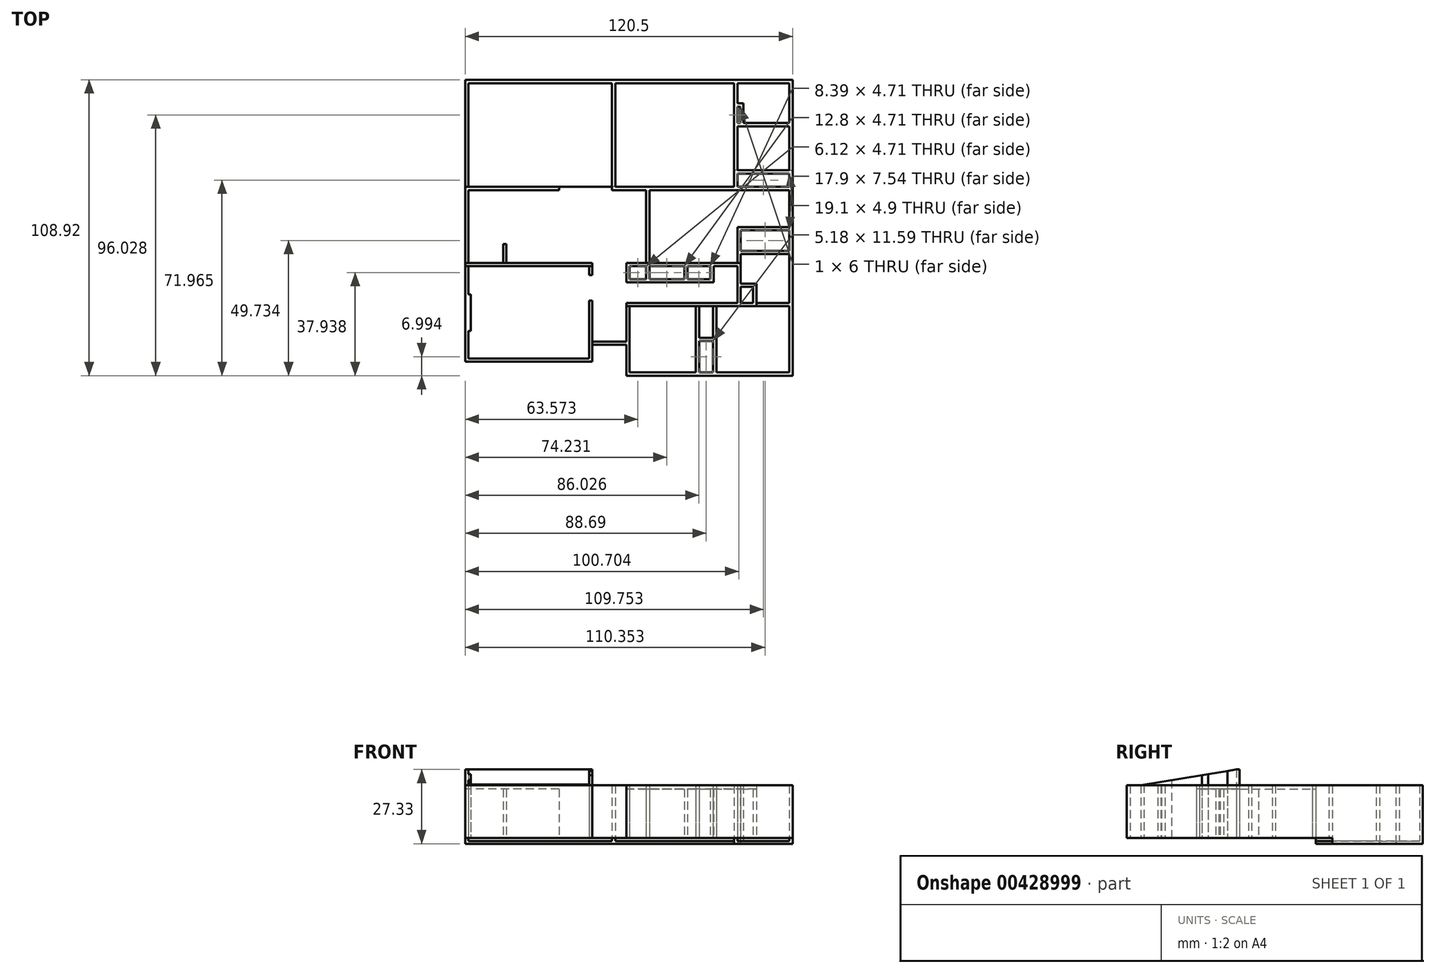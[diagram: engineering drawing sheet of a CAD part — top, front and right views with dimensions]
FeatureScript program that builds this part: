
annotation { "Feature Type Name" : "Feature", "Feature Type Description" : "" }
export const myFeature = defineFeature(function(context is Context, id is Id, definition is map)
    precondition{}
    {
        {
            assignVariable(context, id + "F0", {"name" : "scale", "anyValue" : 125});
        }
        {
            assignVariable(context, id + "F1", {"name" : "sink_depth", "anyValue" : 152.4 * mm / getVariable(context, 'scale')});
        }
        {
            assignVariable(context, id + "F2", {"name" : "ceil_low", "anyValue" : 2247.9 * mm / getVariable(context, 'scale')});
        }
        {
            assignVariable(context, id + "F3", {"name" : "ceil_high", "anyValue" : 2425.7 * mm / getVariable(context, 'scale')});
        }
        {
            assignVariable(context, id + "F4", {"name" : "ceil_max", "anyValue" : (3048 * mm + 101.6 * mm) / getVariable(context, 'scale')});
        }
        {
            var Q0;
            Q0=qCreatedBy(makeId("Top.planeOp"),FACE);
            var sketch = newSketch(context, id + "F5", { "sketchPlane" : qUnion([Q0])});
            skLineSegment(sketch, "E0", {"start": v(0, 0) * mm, "end": v(0, 103.76) * mm});
            skLineSegment(sketch, "E1", {"start": v(0, 103.76) * mm, "end": v(120.5, 103.76) * mm});
            skLineSegment(sketch, "E2", {"start": v(120.5, 103.76) * mm, "end": v(120.5, -5.16) * mm});
            skLineSegment(sketch, "E3", {"start": v(120.5, -5.16) * mm, "end": v(59.32, -5.16) * mm});
            skLineSegment(sketch, "E4", {"start": v(1.2, 1.2) * mm, "end": v(45.6, 1.2) * mm});
            skLineSegment(sketch, "E5", {"start": v(45.6, 1.2) * mm, "end": v(45.6, 22.43) * mm});
            skLineSegment(sketch, "E6", {"start": v(45.6, 22.43) * mm, "end": v(46.8, 22.43) * mm});
            skLineSegment(sketch, "E7", {"start": v(46.8, 22.43) * mm, "end": v(46.8, 7.4) * mm});
            skLineSegment(sketch, "E8", {"start": v(59.32, -3.96) * mm, "end": v(59.32, 6.2) * mm});
            skLineSegment(sketch, "E9", {"start": v(59.32, 21.62) * mm, "end": v(100.2, 21.62) * mm});
            skLineSegment(sketch, "E10", {"start": v(86.1, -3.96) * mm, "end": v(84.9, -3.96) * mm, "construction": true});
            skLineSegment(sketch, "E11", {"start": v(84.9, -3.96) * mm, "end": v(84.9, 20.42) * mm});
            skLineSegment(sketch, "E12", {"start": v(84.9, 20.42) * mm, "end": v(60.52, 20.42) * mm});
            skLineSegment(sketch, "E13", {"start": v(60.52, 20.42) * mm, "end": v(60.52, -3.96) * mm});
            skLineSegment(sketch, "E14", {"start": v(60.52, -3.96) * mm, "end": v(84.9, -3.96) * mm});
            skLineSegment(sketch, "E15", {"start": v(59.32, -3.96) * mm, "end": v(60.52, -3.96) * mm, "construction": true});
            skLineSegment(sketch, "E16", {"start": v(60.52, 20.42) * mm, "end": v(60.52, 21.62) * mm, "construction": true});
            skLineSegment(sketch, "E17", {"start": v(86.1, 20.42) * mm, "end": v(91.28, 20.42) * mm});
            skLineSegment(sketch, "E18", {"start": v(119.3, 20.42) * mm, "end": v(119.3, -3.96) * mm});
            skLineSegment(sketch, "E19", {"start": v(46.8, 1.2) * mm, "end": v(46.8, 0) * mm});
            skLineSegment(sketch, "E20", {"start": v(1.2, 1.2) * mm, "end": v(0, 1.2) * mm, "construction": true});
            skLineSegment(sketch, "E21", {"start": v(1.2, 1.2) * mm, "end": v(1.2, 35.13) * mm});
            skLineSegment(sketch, "E22", {"start": v(1.2, 35.13) * mm, "end": v(45.6, 35.13) * mm});
            skLineSegment(sketch, "E23", {"start": v(45.6, 35.13) * mm, "end": v(45.6, 31.86) * mm});
            skLineSegment(sketch, "E24", {"start": v(45.6, 31.86) * mm, "end": v(46.8, 31.86) * mm});
            skLineSegment(sketch, "E25", {"start": v(46.8, 31.86) * mm, "end": v(46.8, 36.33) * mm});
            skLineSegment(sketch, "E26", {"start": v(15.2, 36.33) * mm, "end": v(15.2, 43.34) * mm});
            skLineSegment(sketch, "E27", {"start": v(15.2, 43.34) * mm, "end": v(14, 43.34) * mm});
            skLineSegment(sketch, "E28", {"start": v(14, 43.34) * mm, "end": v(14, 36.33) * mm});
            skLineSegment(sketch, "E29", {"start": v(14, 36.33) * mm, "end": v(1.2, 36.33) * mm});
            skLineSegment(sketch, "E30", {"start": v(1.2, 36.33) * mm, "end": v(1.2, 63.16) * mm});
            skLineSegment(sketch, "E31", {"start": v(1.2, 63.16) * mm, "end": v(34.52, 63.16) * mm});
            skLineSegment(sketch, "E32", {"start": v(34.52, 63.16) * mm, "end": v(34.52, 64.36) * mm});
            skLineSegment(sketch, "E33", {"start": v(34.52, 64.36) * mm, "end": v(1.2, 64.36) * mm});
            skLineSegment(sketch, "E34", {"start": v(1.2, 64.36) * mm, "end": v(1.2, 102.56) * mm});
            skLineSegment(sketch, "E35", {"start": v(1.2, 102.56) * mm, "end": v(54.03, 102.56) * mm});
            skLineSegment(sketch, "E36", {"start": v(1.2, 36.33) * mm, "end": v(1.2, 35.13) * mm, "construction": true});
            skLineSegment(sketch, "E37", {"start": v(46.8, 36.33) * mm, "end": v(15.2, 36.33) * mm});
            skLineSegment(sketch, "E38", {"start": v(54.03, 102.56) * mm, "end": v(54.03, 63.16) * mm});
            skLineSegment(sketch, "E39", {"start": v(54.03, 63.16) * mm, "end": v(66.63, 63.16) * mm});
            skLineSegment(sketch, "E40", {"start": v(66.63, 63.16) * mm, "end": v(66.63, 36.33) * mm});
            skLineSegment(sketch, "E41", {"start": v(66.63, 36.33) * mm, "end": v(59.32, 36.33) * mm});
            skLineSegment(sketch, "E42", {"start": v(59.32, 36.33) * mm, "end": v(59.32, 29.22) * mm});
            skLineSegment(sketch, "E43", {"start": v(1.2, 102.56) * mm, "end": v(1.2, 103.76) * mm, "construction": true});
            skLineSegment(sketch, "E44", {"start": v(54.03, 102.56) * mm, "end": v(55.23, 102.56) * mm, "construction": true});
            skLineSegment(sketch, "E45", {"start": v(55.23, 102.56) * mm, "end": v(99, 102.56) * mm});
            skLineSegment(sketch, "E46", {"start": v(99, 102.56) * mm, "end": v(99, 64.36) * mm});
            skLineSegment(sketch, "E47", {"start": v(99, 64.36) * mm, "end": v(55.23, 64.36) * mm});
            skLineSegment(sketch, "E48", {"start": v(55.23, 64.36) * mm, "end": v(55.23, 102.56) * mm});
            skLineSegment(sketch, "E49", {"start": v(100.2, 102.56) * mm, "end": v(119.3, 102.56) * mm});
            skLineSegment(sketch, "E50", {"start": v(119.3, 102.56) * mm, "end": v(119.3, 87.87) * mm});
            skLineSegment(sketch, "E51", {"start": v(119.3, 86.67) * mm, "end": v(102.4, 86.67) * mm});
            skLineSegment(sketch, "E52", {"start": v(102.4, 87.87) * mm, "end": v(102.4, 95.07) * mm});
            skLineSegment(sketch, "E53", {"start": v(102.4, 95.07) * mm, "end": v(100.2, 95.07) * mm});
            skLineSegment(sketch, "E54", {"start": v(100.2, 95.07) * mm, "end": v(100.2, 102.56) * mm});
            skLineSegment(sketch, "E55", {"start": v(99, 93.87) * mm, "end": v(101.2, 93.87) * mm});
            skLineSegment(sketch, "E56", {"start": v(101.2, 93.87) * mm, "end": v(101.2, 87.87) * mm});
            skLineSegment(sketch, "E57", {"start": v(101.2, 87.87) * mm, "end": v(99, 87.87) * mm});
            skLineSegment(sketch, "E58", {"start": v(100.2, 102.56) * mm, "end": v(99, 102.56) * mm, "construction": true});
            skLineSegment(sketch, "E59", {"start": v(101.2, 93.87) * mm, "end": v(102.4, 93.87) * mm, "construction": true});
            skLineSegment(sketch, "E60", {"start": v(101.2, 93.87) * mm, "end": v(101.2, 95.07) * mm, "construction": true});
            skLineSegment(sketch, "E61", {"start": v(102.4, 86.67) * mm, "end": v(100.2, 86.67) * mm});
            skLineSegment(sketch, "E62", {"start": v(100.2, 86.67) * mm, "end": v(100.2, 70.45) * mm});
            skLineSegment(sketch, "E63", {"start": v(101.2, 87.87) * mm, "end": v(101.2, 86.67) * mm, "construction": true});
            skLineSegment(sketch, "E64", {"start": v(34.52, 63.16) * mm, "end": v(54.03, 63.16) * mm, "construction": true});
            skLineSegment(sketch, "E65", {"start": v(46.8, 36.33) * mm, "end": v(59.32, 36.33) * mm, "construction": true});
            skLineSegment(sketch, "E66", {"start": v(102.4, 87.87) * mm, "end": v(119.3, 87.87) * mm});
            skLineSegment(sketch, "E67", {"start": v(119.3, 86.67) * mm, "end": v(119.3, 70.45) * mm});
            skLineSegment(sketch, "E68", {"start": v(119.3, 70.45) * mm, "end": v(100.2, 70.45) * mm});
            skLineSegment(sketch, "E69", {"start": v(100.2, 70.45) * mm, "end": v(100.2, 69.25) * mm, "construction": true});
            skLineSegment(sketch, "E70", {"start": v(100.2, 69.25) * mm, "end": v(100.2, 64.36) * mm});
            skLineSegment(sketch, "E71", {"start": v(100.2, 64.36) * mm, "end": v(119.3, 64.36) * mm});
            skLineSegment(sketch, "E72", {"start": v(119.3, 64.36) * mm, "end": v(119.3, 69.25) * mm});
            skLineSegment(sketch, "E73", {"start": v(119.3, 69.25) * mm, "end": v(100.2, 69.25) * mm});
            skLineSegment(sketch, "E74", {"start": v(119.3, 63.16) * mm, "end": v(119.3, 49.54) * mm});
            skLineSegment(sketch, "E75", {"start": v(59.32, 29.22) * mm, "end": v(91.42, 29.22) * mm});
            skLineSegment(sketch, "E76", {"start": v(60.52, 35.13) * mm, "end": v(60.52, 30.42) * mm});
            skLineSegment(sketch, "E77", {"start": v(60.52, 30.42) * mm, "end": v(66.63, 30.42) * mm});
            skLineSegment(sketch, "E78", {"start": v(66.63, 30.42) * mm, "end": v(66.63, 35.13) * mm});
            skLineSegment(sketch, "E79", {"start": v(66.63, 35.13) * mm, "end": v(60.52, 35.13) * mm});
            skLineSegment(sketch, "E80", {"start": v(60.52, 35.13) * mm, "end": v(60.52, 36.33) * mm, "construction": true});
            skLineSegment(sketch, "E81", {"start": v(60.52, 35.13) * mm, "end": v(59.32, 35.13) * mm, "construction": true});
            skLineSegment(sketch, "E82", {"start": v(60.52, 30.42) * mm, "end": v(60.52, 29.22) * mm, "construction": true});
            skLineSegment(sketch, "E83", {"start": v(67.83, 63.16) * mm, "end": v(67.83, 36.33) * mm});
            skLineSegment(sketch, "E84", {"start": v(67.83, 36.33) * mm, "end": v(100.2, 36.33) * mm});
            skLineSegment(sketch, "E85", {"start": v(91.42, 29.22) * mm, "end": v(91.42, 35.13) * mm});
            skLineSegment(sketch, "E86", {"start": v(91.42, 35.13) * mm, "end": v(100.2, 35.13) * mm});
            skLineSegment(sketch, "E87", {"start": v(100.2, 35.13) * mm, "end": v(100.2, 21.62) * mm});
            skLineSegment(sketch, "E88", {"start": v(119.3, 102.56) * mm, "end": v(120.5, 102.56) * mm, "construction": true});
            skLineSegment(sketch, "E89", {"start": v(66.63, 36.33) * mm, "end": v(67.83, 36.33) * mm, "construction": true});
            skLineSegment(sketch, "E90", {"start": v(100.2, 36.33) * mm, "end": v(100.2, 35.13) * mm, "construction": true});
            skLineSegment(sketch, "E91", {"start": v(67.83, 35.13) * mm, "end": v(80.63, 35.13) * mm});
            skLineSegment(sketch, "E92", {"start": v(90.22, 35.13) * mm, "end": v(90.22, 30.42) * mm});
            skLineSegment(sketch, "E93", {"start": v(90.22, 30.42) * mm, "end": v(81.83, 30.42) * mm});
            skLineSegment(sketch, "E94", {"start": v(67.83, 30.42) * mm, "end": v(67.83, 35.13) * mm});
            skLineSegment(sketch, "E95", {"start": v(67.83, 63.16) * mm, "end": v(119.3, 63.16) * mm});
            skLineSegment(sketch, "E96", {"start": v(99, 64.36) * mm, "end": v(99, 63.16) * mm, "construction": true});
            skLineSegment(sketch, "E97", {"start": v(92.48, 20.42) * mm, "end": v(92.48, -3.96) * mm});
            skLineSegment(sketch, "E98", {"start": v(91.28, 20.42) * mm, "end": v(92.48, 20.42) * mm});
            skLineSegment(sketch, "E99", {"start": v(92.48, 20.42) * mm, "end": v(119.3, 20.42) * mm});
            skLineSegment(sketch, "E100.bottom", {"start": v(101.4, 21.62) * mm, "end": v(106.01, 21.62) * mm});
            skLineSegment(sketch, "E100.top", {"start": v(101.4, 27.51) * mm, "end": v(106.01, 27.51) * mm});
            skLineSegment(sketch, "E100.left", {"start": v(101.4, 21.62) * mm, "end": v(101.4, 27.51) * mm});
            skLineSegment(sketch, "E100.right", {"start": v(106.01, 21.62) * mm, "end": v(106.01, 27.51) * mm});
            skLineSegment(sketch, "E101", {"start": v(101.4, 28.71) * mm, "end": v(101.4, 39.6) * mm});
            skLineSegment(sketch, "E102", {"start": v(101.4, 39.6) * mm, "end": v(119.3, 39.6) * mm});
            skLineSegment(sketch, "E103", {"start": v(119.3, 39.6) * mm, "end": v(119.3, 21.62) * mm});
            skLineSegment(sketch, "E104", {"start": v(119.3, 21.62) * mm, "end": v(107.21, 21.62) * mm});
            skLineSegment(sketch, "E105", {"start": v(107.21, 21.62) * mm, "end": v(107.21, 28.71) * mm});
            skLineSegment(sketch, "E106", {"start": v(101.4, 28.71) * mm, "end": v(107.21, 28.71) * mm});
            skLineSegment(sketch, "E107", {"start": v(106.01, 27.51) * mm, "end": v(107.21, 27.51) * mm, "construction": true});
            skLineSegment(sketch, "E108", {"start": v(106.01, 27.51) * mm, "end": v(106.01, 28.71) * mm, "construction": true});
            skLineSegment(sketch, "E109.bottom", {"start": v(101.4, 40.8) * mm, "end": v(119.3, 40.8) * mm});
            skLineSegment(sketch, "E109.top", {"start": v(101.4, 48.34) * mm, "end": v(119.3, 48.34) * mm});
            skLineSegment(sketch, "E109.left", {"start": v(101.4, 40.8) * mm, "end": v(101.4, 48.34) * mm});
            skLineSegment(sketch, "E109.right", {"start": v(119.3, 40.8) * mm, "end": v(119.3, 48.34) * mm});
            skLineSegment(sketch, "E110", {"start": v(119.3, 40.8) * mm, "end": v(119.3, 39.6) * mm, "construction": true});
            skLineSegment(sketch, "E111", {"start": v(119.3, 49.54) * mm, "end": v(119.3, 48.34) * mm, "construction": true});
            skLineSegment(sketch, "E112", {"start": v(100.2, 21.62) * mm, "end": v(101.4, 21.62) * mm, "construction": true});
            skLineSegment(sketch, "E113", {"start": v(81.83, 35.13) * mm, "end": v(81.83, 30.42) * mm});
            skLineSegment(sketch, "E114", {"start": v(80.63, 30.42) * mm, "end": v(80.63, 30.42) * mm});
            skLineSegment(sketch, "E115", {"start": v(81.83, 35.13) * mm, "end": v(90.22, 35.13) * mm});
            skLineSegment(sketch, "E116", {"start": v(80.63, 35.13) * mm, "end": v(81.83, 35.13) * mm, "construction": true});
            skLineSegment(sketch, "E117", {"start": v(90.22, 35.13) * mm, "end": v(91.42, 35.13) * mm, "construction": true});
            skLineSegment(sketch, "E118", {"start": v(120.5, -5.16) * mm, "end": v(120.5, -45.16) * mm});
            skLineSegment(sketch, "E119", {"start": v(120.5, -45.16) * mm, "end": v(59.32, -45.16) * mm});
            skLineSegment(sketch, "E120", {"start": v(59.32, -45.16) * mm, "end": v(59.32, -5.16) * mm});
            skLineSegment(sketch, "E121", {"start": v(60.52, -5.16) * mm, "end": v(60.52, -43.96) * mm});
            skLineSegment(sketch, "E122", {"start": v(60.52, -43.96) * mm, "end": v(119.3, -43.96) * mm});
            skLineSegment(sketch, "E123", {"start": v(119.3, -43.96) * mm, "end": v(119.3, -5.16) * mm});
            skLineSegment(sketch, "E124", {"start": v(60.52, -43.96) * mm, "end": v(60.52, -45.16) * mm, "construction": true});
            skLineSegment(sketch, "E125", {"start": v(60.52, -43.96) * mm, "end": v(59.32, -43.96) * mm, "construction": true});
            skLineSegment(sketch, "E126", {"start": v(59.32, -3.96) * mm, "end": v(59.32, -5.16) * mm});
            skLineSegment(sketch, "E127.trimOffspring", {"start": v(46.8, 0) * mm, "end": v(0, 0) * mm});
            skLineSegment(sketch, "E128", {"start": v(46.8, 6.2) * mm, "end": v(59.32, 6.2) * mm});
            skLineSegment(sketch, "E129", {"start": v(59.32, 7.4) * mm, "end": v(46.8, 7.4) * mm});
            skLineSegment(sketch, "E130", {"start": v(46.8, 7.4) * mm, "end": v(46.8, 6.2) * mm, "construction": true});
            skLineSegment(sketch, "E131", {"start": v(46.8, 6.2) * mm, "end": v(46.8, 1.2) * mm});
            skLineSegment(sketch, "E132", {"start": v(59.32, 6.2) * mm, "end": v(59.32, 7.4) * mm, "construction": true});
            skLineSegment(sketch, "E133", {"start": v(59.32, 7.4) * mm, "end": v(59.32, 21.62) * mm});
            skLineSegment(sketch, "E134", {"start": v(1.2, 1.2) * mm, "end": v(1.2, 0) * mm, "construction": true});
            skLineSegment(sketch, "E135", {"start": v(80.63, 35.13) * mm, "end": v(80.63, 30.42) * mm});
            skLineSegment(sketch, "E136", {"start": v(80.63, 30.42) * mm, "end": v(67.83, 30.42) * mm});
            skLineSegment(sketch, "E137", {"start": v(1.2, 11.36) * mm, "end": v(2.01, 11.36) * mm});
            skLineSegment(sketch, "E138", {"start": v(2.01, 11.36) * mm, "end": v(2.01, 24.77) * mm});
            skLineSegment(sketch, "E139", {"start": v(2.01, 24.77) * mm, "end": v(1.2, 24.77) * mm});
            skLineSegment(sketch, "E140", {"start": v(18.07, 103.76) * mm, "end": v(18.07, 102.56) * mm});
            skLineSegment(sketch, "E141", {"start": v(37.57, 103.76) * mm, "end": v(37.57, 102.56) * mm});
            skLineSegment(sketch, "E142", {"start": v(18.78, 64.36) * mm, "end": v(18.78, 63.16) * mm, "construction": true});
            skLineSegment(sketch, "E143", {"start": v(30.7, 64.36) * mm, "end": v(30.7, 63.16) * mm, "construction": true});
            skLineSegment(sketch, "E144", {"start": v(91.28, 20.42) * mm, "end": v(91.28, 8.83) * mm});
            skLineSegment(sketch, "E145", {"start": v(91.28, -3.96) * mm, "end": v(92.48, -3.96) * mm});
            skLineSegment(sketch, "E146", {"start": v(119.3, -3.96) * mm, "end": v(92.48, -3.96) * mm});
            skLineSegment(sketch, "E147", {"start": v(91.28, -3.96) * mm, "end": v(86.1, -3.96) * mm});
            skLineSegment(sketch, "E148", {"start": v(86.1, 8.83) * mm, "end": v(91.28, 8.83) * mm});
            skLineSegment(sketch, "E149", {"start": v(86.1, 8.83) * mm, "end": v(86.1, 20.42) * mm});
            skLineSegment(sketch, "E150", {"start": v(91.28, 8.83) * mm, "end": v(91.28, 7.63) * mm, "construction": true});
            skLineSegment(sketch, "E151", {"start": v(91.28, 7.63) * mm, "end": v(91.28, -3.96) * mm});
            skLineSegment(sketch, "E152", {"start": v(86.1, 7.63) * mm, "end": v(86.1, 8.83) * mm, "construction": true});
            skLineSegment(sketch, "E153", {"start": v(86.1, 7.63) * mm, "end": v(86.1, -3.96) * mm});
            skLineSegment(sketch, "E154", {"start": v(86.1, 7.63) * mm, "end": v(91.28, 7.63) * mm});
            skLineSegment(sketch, "E155", {"start": v(100.2, 36.33) * mm, "end": v(100.2, 49.54) * mm});
            skLineSegment(sketch, "E156", {"start": v(100.2, 49.54) * mm, "end": v(119.3, 49.54) * mm});
            skLineSegment(sketch, "E157", {"start": v(1.2, 36.33) * mm, "end": v(0, 36.33) * mm});
            skLineSegment(sketch, "E158", {"start": v(46.8, 7.4) * mm, "end": v(46.8, 6.2) * mm});
            skLineSegment(sketch, "E159", {"start": v(15.2, 36.33) * mm, "end": v(14, 36.33) * mm});
            skLineSegment(sketch, "E160", {"start": v(66.63, 36.33) * mm, "end": v(67.83, 36.33) * mm});
            skLineSegment(sketch, "E161", {"start": v(60.52, 20.42) * mm, "end": v(59.32, 20.42) * mm});
            skLineSegment(sketch, "E162", {"start": v(86.1, 20.42) * mm, "end": v(84.9, 20.42) * mm});
            skLineSegment(sketch, "E163", {"start": v(100.2, 36.33) * mm, "end": v(101.4, 36.33) * mm});
            skLineSegment(sketch, "E164", {"start": v(107.21, 21.62) * mm, "end": v(107.21, 20.42) * mm});
            skLineSegment(sketch, "E165", {"start": v(1.2, 64.36) * mm, "end": v(0, 64.36) * mm});
            skLineSegment(sketch, "E166", {"start": v(100.2, 93.87) * mm, "end": v(100.2, 87.87) * mm});
            skLineSegment(sketch, "E167", {"start": v(55.23, 64.36) * mm, "end": v(54.03, 64.36) * mm});
            skLineSegment(sketch, "E168", {"start": v(100.2, 70.45) * mm, "end": v(99, 70.45) * mm});
            skLineSegment(sketch, "E169", {"start": v(119.3, 70.45) * mm, "end": v(120.5, 70.45) * mm});
            skSolve(sketch);
        }
        {
            var Q0;
            {var subQ7=sQuery(id+"F5.wireOp",EDGE,"E4");Q0=makeQuery(id+"F5.imprint","IMPRINT",FACE,{"disambiguationData":[TD([[makeQuery(id+"F5.imprint","IMPRINT",EDGE,{"derivedFrom":subQ7}),-1.0]])]});}
            var Q1;
            {var subQ0=sQuery(id+"F5.wireOp",EDGE,"E137");Q1=makeQuery(id+"F5.imprint","IMPRINT",FACE,{"disambiguationData":[TD([[makeQuery(id+"F5.imprint","IMPRINT",EDGE,{"derivedFrom":subQ0}),1.0]])]});}
            extrude(context, id + "F6", {"entities" : qUnion([Q0, Q1]), "depth" : getVariable(context, 'ceil_max')});
        }
        {
            var Q0;
            Q0=makeQuery(id+"F6.opExtrude","SWEPT_FACE",FACE,{"disambiguationData":[OSD([sQuery(id+"F5.wireOp",EDGE,"E0")])]});
            var sketch = newSketch(context, id + "F7", { "sketchPlane" : qUnion([Q0])});
            skPoint(sketch, "E170.0", {"position": v(-35.13, 25.2) * mm});
            skLineSegment(sketch, "E171", {"start": v(0, 19.4) * mm, "end": v(0, 25.2) * mm});
            skLineSegment(sketch, "E172", {"start": v(0, 25.2) * mm, "end": v(-35.13, 25.2) * mm});
            skLineSegment(sketch, "E173", {"start": v(0, 19.4) * mm, "end": v(-35.13, 25.2) * mm});
            skSolve(sketch);
        }
        {
            var Q0;
            Q0 = qSketchRegion(id + "F7", true);
            extrude(context, id + "F8", {"entities" : qUnion([Q0]), "operationType" : NewBodyOperationType.REMOVE, "endBound" : BoundingType.THROUGH_ALL, "oppositeDirection" : true, "depth" : 25 * mm});
        }
        {
            var Q0;
            {var subQ1=sQuery(id+"F5.wireOp",EDGE,"E34");Q0=makeQuery(id+"F5.imprint","IMPRINT",FACE,{"disambiguationData":[TD([[makeQuery(id+"F5.imprint","IMPRINT",EDGE,{"derivedFrom":subQ1}),1.0]])]});}
            var Q1;
            {var subQ0=sQuery(id+"F5.wireOp",EDGE,"E140");Q1=makeQuery(id+"F5.imprint","IMPRINT",FACE,{"disambiguationData":[TD([[makeQuery(id+"F5.imprint","IMPRINT",EDGE,{"derivedFrom":subQ0}),1.0]])]});}
            var Q2;
            {var subQ11=sQuery(id+"F5.wireOp",EDGE,"E2");Q2=makeQuery(id+"F5.imprint","IMPRINT",FACE,{"disambiguationData":[TD([[makeQuery(id+"F5.imprint","IMPRINT",EDGE,{"derivedFrom":subQ11}),-1.0]])]});}
            var Q3;
            {var subQ5=sQuery(id+"F5.wireOp",EDGE,"E166");Q3=makeQuery(id+"F5.imprint","IMPRINT",FACE,{"disambiguationData":[TD([[makeQuery(id+"F5.imprint","IMPRINT",EDGE,{"derivedFrom":subQ5}),-1.0]])]});}
            var Q4;
            Q4=makeQuery(id+"F5.imprint","IMPRINT",FACE,{"disambiguationData":[TD([[makeQuery(id+"F5.imprint","IMPRINT",EDGE,{"derivedFrom":sQuery(id+"F5.wireOp",EDGE,"E8")}),-1.0]])]});
            extrude(context, id + "F9", {"entities" : qUnion([Q0, Q1, Q2, Q3, Q4]), "operationType" : NewBodyOperationType.ADD, "depth" : getVariable(context, 'ceil_high')});
        }
        {
            var Q0;
            Q0=makeQuery(id+"F5.imprint","IMPRINT",FACE,{"disambiguationData":[TD([[makeQuery(id+"F5.imprint","IMPRINT",EDGE,{"derivedFrom":sQuery(id+"F5.wireOp",EDGE,"E30")}),1.0]])]});
            var Q1;
            {var subQ3=sQuery(id+"F5.wireOp",EDGE,"E9");Q1=makeQuery(id+"F5.imprint","IMPRINT",FACE,{"disambiguationData":[TD([[makeQuery(id+"F5.imprint","IMPRINT",EDGE,{"derivedFrom":subQ3}),-1.0]])]});}
            var Q2;
            Q2=makeQuery(id+"F5.imprint","IMPRINT",FACE,{"disambiguationData":[TD([[makeQuery(id+"F5.imprint","IMPRINT",EDGE,{"derivedFrom":sQuery(id+"F5.wireOp",EDGE,"E26")}),1.0]])]});
            extrude(context, id + "F10", {"entities" : qUnion([Q0, Q1, Q2]), "operationType" : NewBodyOperationType.ADD, "depth" : getVariable(context, 'ceil_low')});
        }
        {
            var Q0;
            {var subQ19=sQuery(id+"F5.wireOp",EDGE,"E45");Q0=makeQuery(id+"F5.imprint","IMPRINT",FACE,{"disambiguationData":[TD([[makeQuery(id+"F5.imprint","IMPRINT",EDGE,{"derivedFrom":subQ19}),1.0]])]});}
            var Q1;
            {var subQ0=sQuery(id+"F5.wireOp",EDGE,"E140");Q1=makeQuery(id+"F5.imprint","IMPRINT",FACE,{"disambiguationData":[TD([[makeQuery(id+"F5.imprint","IMPRINT",EDGE,{"derivedFrom":subQ0}),1.0]])]});}
            var Q2;
            {var subQ1=sQuery(id+"F5.wireOp",EDGE,"E34");Q2=makeQuery(id+"F5.imprint","IMPRINT",FACE,{"disambiguationData":[TD([[makeQuery(id+"F5.imprint","IMPRINT",EDGE,{"derivedFrom":subQ1}),1.0]])]});}
            var Q3;
            {var subQ5=sQuery(id+"F5.wireOp",EDGE,"E166");Q3=makeQuery(id+"F5.imprint","IMPRINT",FACE,{"disambiguationData":[TD([[makeQuery(id+"F5.imprint","IMPRINT",EDGE,{"derivedFrom":subQ5}),-1.0]])]});}
            extrude(context, id + "F11", {"entities" : qUnion([Q0, Q1, Q2, Q3]), "operationType" : NewBodyOperationType.ADD, "oppositeDirection" : true, "depth" : getVariable(context, 'sink_depth')});
        }
        {
            var Q0;
            Q0=makeQuery(id+"F11.opExtrude","CAP_FACE",FACE,{"disambiguationData":[OSD([sQuery(id+"F5.wireOp",EDGE,"E0"),sQuery(id+"F5.wireOp",EDGE,"E1"),sQuery(id+"F5.wireOp",EDGE,"E2"),sQuery(id+"F5.wireOp",EDGE,"E34"),sQuery(id+"F5.wireOp",EDGE,"E35"),sQuery(id+"F5.wireOp",EDGE,"E38"),sQuery(id+"F5.wireOp",EDGE,"E45"),sQuery(id+"F5.wireOp",EDGE,"E46"),sQuery(id+"F5.wireOp",EDGE,"E48"),sQuery(id+"F5.wireOp",EDGE,"E49"),sQuery(id+"F5.wireOp",EDGE,"E50"),sQuery(id+"F5.wireOp",EDGE,"E51"),sQuery(id+"F5.wireOp",EDGE,"E52"),sQuery(id+"F5.wireOp",EDGE,"E53"),sQuery(id+"F5.wireOp",EDGE,"E54"),sQuery(id+"F5.wireOp",EDGE,"E55"),sQuery(id+"F5.wireOp",EDGE,"E56"),sQuery(id+"F5.wireOp",EDGE,"E57"),sQuery(id+"F5.wireOp",EDGE,"E61"),sQuery(id+"F5.wireOp",EDGE,"E62"),sQuery(id+"F5.wireOp",EDGE,"E66"),sQuery(id+"F5.wireOp",EDGE,"E67"),sQuery(id+"F5.wireOp",EDGE,"E165"),sQuery(id+"F5.wireOp",EDGE,"E167"),sQuery(id+"F5.wireOp",EDGE,"E168"),sQuery(id+"F5.wireOp",EDGE,"E169")])],"isStart":false});
            var sketch = newSketch(context, id + "F12", { "sketchPlane" : qUnion([Q0])});
            skPoint(sketch, "E174.0", {"position": v(120.5, -70.45) * mm});
            skPoint(sketch, "E175.0", {"position": v(99, -70.45) * mm});
            skPoint(sketch, "E176.0", {"position": v(0, -64.36) * mm});
            skPoint(sketch, "E177.0", {"position": v(0, -103.76) * mm});
            skPoint(sketch, "E178.0", {"position": v(120.5, -103.76) * mm});
            skLineSegment(sketch, "E179", {"start": v(0, -64.36) * mm, "end": v(99, -64.36) * mm});
            skLineSegment(sketch, "E180", {"start": v(99, -64.36) * mm, "end": v(99, -70.45) * mm});
            skLineSegment(sketch, "E181", {"start": v(120.5, -70.45) * mm, "end": v(120.5, -103.76) * mm});
            skLineSegment(sketch, "E182", {"start": v(0, -103.76) * mm, "end": v(0, -64.36) * mm});
            skLineSegment(sketch, "E183", {"start": v(120.5, -70.45) * mm, "end": v(99, -70.45) * mm});
            skSolve(sketch);
        }
        {
            var Q0;
            {var subQ1=makeQuery(id+"F11.opExtrude","CAP_EDGE",EDGE,{"disambiguationData":[OSD([sQuery(id+"F5.wireOp",EDGE,"E34")])],"isStart":false});Q0=makeQuery(id+"F12.imprint","IMPRINT",FACE,{"disambiguationData":[TD([[makeQuery(id+"F12.imprint","IMPRINT",EDGE,{"derivedFrom":subQ1}),1.0]])]});}
            var Q1;
            {var subQ3=sQuery(id+"F12.wireOp",EDGE,"E180");Q1=makeQuery(id+"F12.imprint","IMPRINT",FACE,{"disambiguationData":[TD([[makeQuery(id+"F12.imprint","IMPRINT",EDGE,{"derivedFrom":subQ3}),-1.0]])]});}
            var Q2;
            {var subQ6=sQuery(id+"F12.wireOp",EDGE,"E181");Q2=makeQuery(id+"F12.imprint","IMPRINT",FACE,{"disambiguationData":[TD([[makeQuery(id+"F12.imprint","IMPRINT",EDGE,{"derivedFrom":subQ6}),1.0]])]});}
            var Q3;
            {var subQ1=makeQuery(id+"F11.opExtrude","CAP_EDGE",EDGE,{"disambiguationData":[OSD([sQuery(id+"F5.wireOp",EDGE,"E62")])],"isStart":false});Q3=makeQuery(id+"F12.imprint","IMPRINT",FACE,{"disambiguationData":[TD([[makeQuery(id+"F12.imprint","IMPRINT",EDGE,{"derivedFrom":subQ1}),-1.0]])]});}
            var Q4;
            Q4=makeQuery(id+"F12.imprint","IMPRINT",FACE,{"disambiguationData":[TD([[makeQuery(id+"F12.imprint","IMPRINT",EDGE,{"derivedFrom":makeQuery(id+"F11.opExtrude","CAP_EDGE",EDGE,{"disambiguationData":[OSD([sQuery(id+"F5.wireOp",EDGE,"E49")])],"isStart":false})}),1.0]])]});
            extrude(context, id + "F13", {"entities" : qUnion([Q0, Q1, Q2, Q3, Q4]), "operationType" : NewBodyOperationType.ADD, "depth" : 0.91 * mm});
        }
    });
